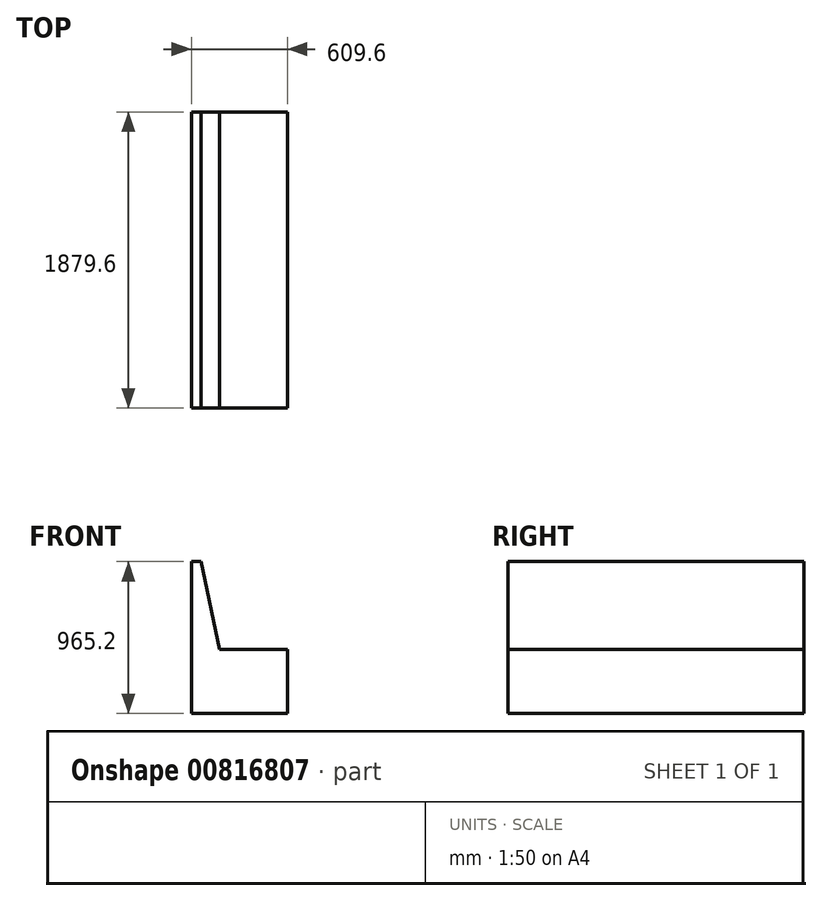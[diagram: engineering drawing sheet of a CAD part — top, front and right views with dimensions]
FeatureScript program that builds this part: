
annotation { "Feature Type Name" : "Feature", "Feature Type Description" : "" }
export const myFeature = defineFeature(function(context is Context, id is Id, definition is map)
    precondition{}
    {
        {
            var Q0;
            Q0=qCreatedBy(makeId("Front.planeOp"),FACE);
            var sketch = newSketch(context, id + "F0", { "sketchPlane" : qUnion([Q0])});
            skLineSegment(sketch, "E0", {"start": v(-196.07, -390.52) * mm, "end": v(-196.07, 574.68) * mm});
            skLineSegment(sketch, "E1", {"start": v(-196.07, 574.68) * mm, "end": v(-132.57, 574.68) * mm});
            skLineSegment(sketch, "E2", {"start": v(-196.07, -390.52) * mm, "end": v(413.53, -390.52) * mm});
            skLineSegment(sketch, "E3", {"start": v(413.53, -390.52) * mm, "end": v(413.53, 15.88) * mm});
            skLineSegment(sketch, "E4", {"start": v(413.53, 15.88) * mm, "end": v(-18.27, 15.88) * mm});
            skLineSegment(sketch, "E5", {"start": v(-18.27, 15.88) * mm, "end": v(-132.57, 574.68) * mm});
            skSolve(sketch);
        }
        {
            var Q0;
            Q0=makeQuery(id+"F0.imprint","IMPRINT",FACE,{"disambiguationData":[TD([[makeQuery(id+"F0.imprint","IMPRINT",EDGE,{"derivedFrom":sQuery(id+"F0.wireOp",EDGE,"E0")}),-1.0]])]});
            extrude(context, id + "F1", {"entities" : qUnion([Q0]), "depth" : 1879.6 * mm, "offsetDistance" : 25.4 * mm});
        }
    });
